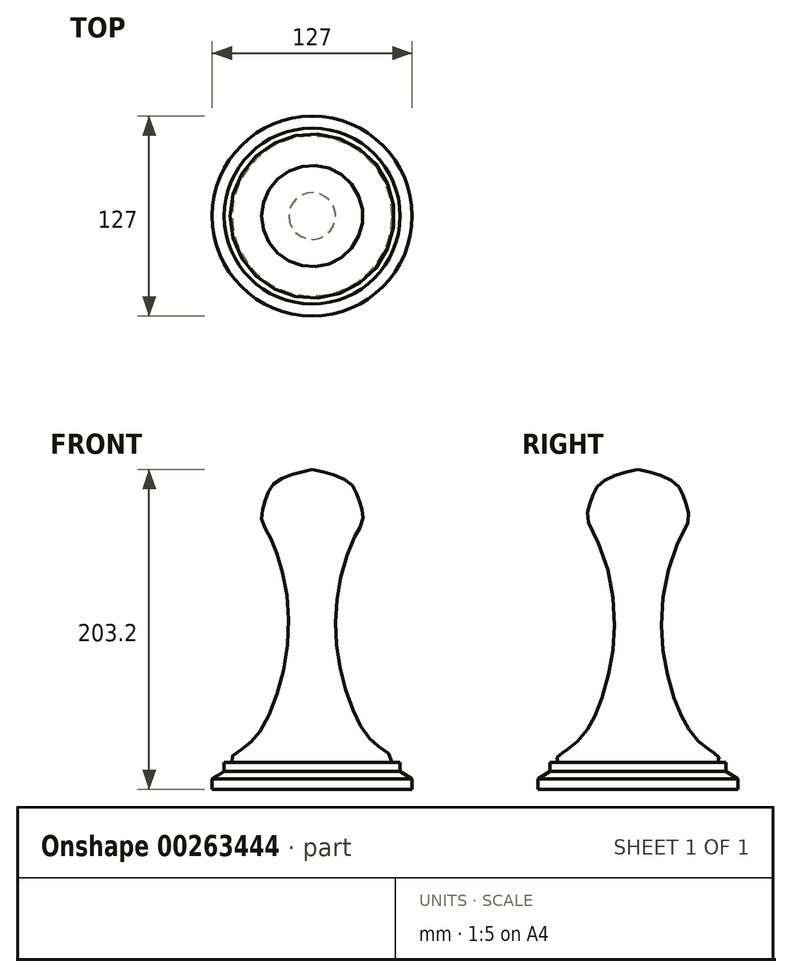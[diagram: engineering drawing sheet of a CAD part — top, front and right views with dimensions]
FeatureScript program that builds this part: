
annotation { "Feature Type Name" : "Feature", "Feature Type Description" : "" }
export const myFeature = defineFeature(function(context is Context, id is Id, definition is map)
    precondition{}
    {
        {
            var Q0;
            Q0=qCreatedBy(makeId("Front.planeOp"),FACE);
            var sketch = newSketch(context, id + "F0", { "sketchPlane" : qUnion([Q0])});
            skLineSegment(sketch, "E0", {"start": v(0, -96.87) * mm, "end": v(-63.5, -96.87) * mm});
            skLineSegment(sketch, "E1", {"start": v(-63.5, -96.87) * mm, "end": v(-63.5, -90.18) * mm});
            skLineSegment(sketch, "E2", {"start": v(-63.5, -90.18) * mm, "end": v(-55.86, -85.4) * mm});
            skLineSegment(sketch, "E3", {"start": v(-55.86, -85.4) * mm, "end": v(-55.86, -79.67) * mm});
            skLineSegment(sketch, "E4", {"start": v(-55.86, -79.67) * mm, "end": v(-50.76, -79.67) * mm});
            skFitSpline(sketch, "E5", {"points": [v(-50.76, -79.67) * mm, v(-48.39, -73.93) * mm, v(-33.42, -60.56) * mm, v(-14.95, 3.14) * mm, v(-25.46, 60.47) * mm, v(-32.14, 75.12) * mm, v(-29.92, 86.27) * mm, v(-25.14, 96.46) * mm, v(-13.67, 102.83) * mm, v(0, 106.33) * mm], "startDerivative": vector(-150.89, 75.95) * mm, "endDerivative": vector(150.84, 33.01) * mm});
            skLineSegment(sketch, "E6", {"start": v(0, -96.87) * mm, "end": v(0, 106.33) * mm});
            skSolve(sketch);
        }
        {
            var Q0;
            Q0=makeQuery(id+"F0.imprint","IMPRINT",FACE,{"disambiguationData":[TD([[makeQuery(id+"F0.imprint","IMPRINT",EDGE,{"derivedFrom":sQuery(id+"F0.wireOp",EDGE,"E0")}),-1.0]])]});
            var Q1;
            Q1=sQuery(id+"F0.wireOp",EDGE,"E6");
            revolve(context, id + "F1", {"entities" : qUnion([Q0]), "axis" : qUnion([Q1]), "revolveType" : RevolveType.FULL});
        }
    });
